# Revit family: Haworth_Janus_Titan_SquareTelescope_197
name_source: partatom
category: Furniture
revit_build: Autodesk Revit 2018 (Build: 20170223_1515(x64)
units: mm (PartAtom-declared; Revit-internal decimal feet)

## family parameters
Always vertical = Yes
Cut with Voids When Loaded = No
OmniClass Number = 23.40.70.14.64.21
OmniClass Title = Systems Furniture
Room Calculation Point = No
Shared = No
Work Plane-Based = No

## types (2) — shared parameters
Actual Depth = 197"
Actual Height = 114"
Actual Width = 197"
Assembly Code = E2020200
Base Depth = 1"
Base Height = 85 1/4"
Canopy Height = 28 3/4"
Fitting Finish = Haworth _ Polymer _ Black
Manufacturer = Haworth
Model = HCJC-JT-UEQJ7S
Revision Number = 1
Round Base Radius = 18"
Size = Verify Final Dim. w/ Haworth
Square Base Wide = 36"
URL = http://www.haworth.com
URL - Product = https://www.haworth.com
Warranty = http://www.haworth.com

## per-type parameters (varying)
| type | Description |
| Square Base | Haworth - Janus Titan - Square Telescope Umbrella - 197" - Square Base |
| Mount Base | Haworth - Janus Titan - Square Telescope Umbrella - 197" - Mount Base |

type visibility flags: 2 boolean params named "<type name>" — each type sets only its own to Yes (folded from table)

## geometry (parser evidence)
native form markers: Sweep x7
no freeform markers — native parametric forms only
